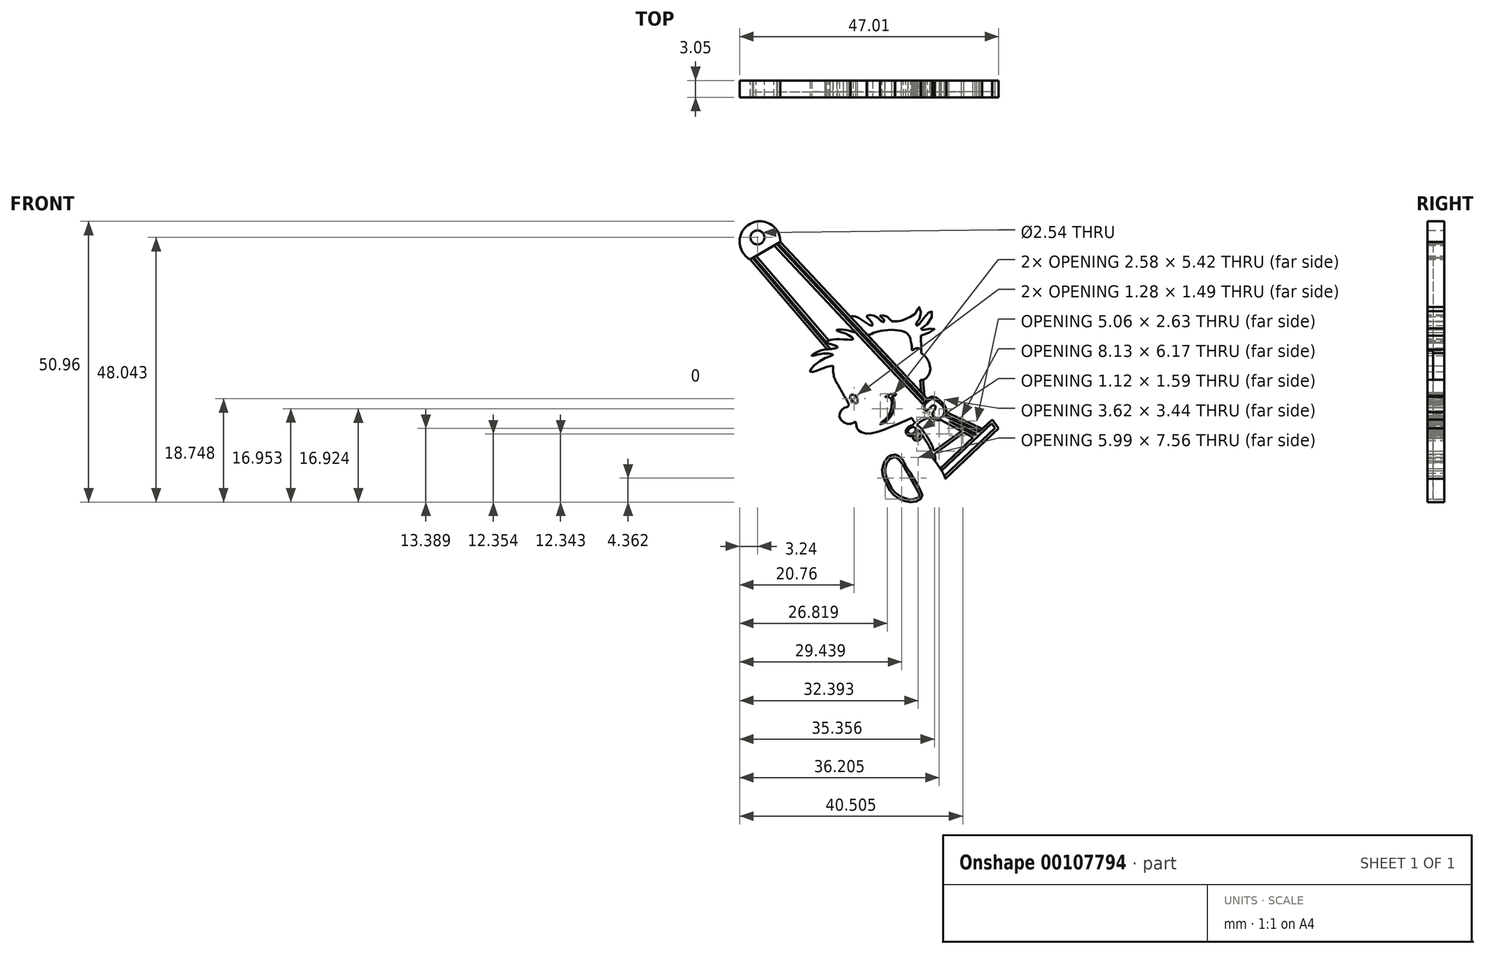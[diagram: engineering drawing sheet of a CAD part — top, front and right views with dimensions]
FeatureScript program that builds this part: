
annotation { "Feature Type Name" : "Feature", "Feature Type Description" : "" }
export const myFeature = defineFeature(function(context is Context, id is Id, definition is map)
    precondition{}
    {
        {
            var Q0;
            Q0=qCreatedBy(makeId("Front.planeOp"),FACE);
            var sketch = newSketch(context, id + "F0", { "sketchPlane" : qUnion([Q0])});
            skLineSegment(sketch, "E0", {"start": v(-64.2, 41.48) * mm, "end": v(-50.25, 25.18) * mm});
            skLineSegment(sketch, "E1", {"start": v(-64.2, 41.48) * mm, "end": v(-58.72, 44.68) * mm});
            skLineSegment(sketch, "E2", {"start": v(-63.09, 42.13) * mm, "end": v(-49.93, 26.76) * mm});
            skLineSegment(sketch, "E3", {"start": v(-58.72, 44.68) * mm, "end": v(-31.98, 16.16) * mm});
            skLineSegment(sketch, "E4", {"start": v(-59.84, 44.02) * mm, "end": v(-32.85, 15.22) * mm});
            skFitSpline(sketch, "E5", {"points": [v(-47.25, 16.86) * mm, v(-48.32, 18.85) * mm, v(-48.92, 20.02) * mm, v(-49.14, 21.44) * mm, v(-49.14, 22.23) * mm], "startDerivative": vector(-3.2, 6.96) * mm, "endDerivative": vector(0.11, 3.82) * mm});
            skFitSpline(sketch, "E6", {"points": [v(-49.14, 22.23) * mm, v(-50.63, 21.88) * mm, v(-53.28, 21.09) * mm, v(-51.32, 23.2) * mm, v(-49.14, 24.21) * mm, v(-51.26, 24.37) * mm, v(-53.02, 24.02) * mm, v(-51.6, 24.88) * mm, v(-50.25, 25.18) * mm], "startDerivative": vector(-10.95, -1.4) * mm, "endDerivative": vector(11.55, 1.04) * mm});
            skFitSpline(sketch, "E7", {"points": [v(-50.63, 26.4) * mm, v(-49.73, 26.15) * mm, v(-48.34, 25.57) * mm, v(-50.25, 25.18) * mm], "startDerivative": vector(2.9, -0.35) * mm, "endDerivative": vector(-7.58, -0.71) * mm});
            skFitSpline(sketch, "E8", {"points": [v(-50.63, 26.4) * mm, v(-49.93, 26.76) * mm, v(-48.12, 27.02) * mm, v(-45.52, 27.03) * mm, v(-46.81, 28) * mm, v(-48.51, 28.64) * mm, v(-47.59, 28.77) * mm, v(-45.03, 28.22) * mm], "startDerivative": vector(6.97, 4.48) * mm, "endDerivative": vector(15.06, -4.13) * mm});
            skFitSpline(sketch, "E9", {"points": [v(-45.97, 31.08) * mm, v(-45.52, 31.23) * mm, v(-44.43, 30.84) * mm, v(-42.05, 29.46) * mm, v(-42.28, 30.32) * mm, v(-43.07, 31.14) * mm, v(-42.61, 31.42) * mm, v(-41.12, 30.96) * mm, v(-40.04, 30.12) * mm, v(-39.85, 30.51) * mm, v(-40.62, 31.22) * mm, v(-39.61, 31.25) * mm, v(-38.58, 30.32) * mm, v(-37.9, 30.27) * mm], "startDerivative": vector(8.3, 3.64) * mm, "endDerivative": vector(15.52, 2.77) * mm});
            skFitSpline(sketch, "E10", {"points": [v(-37.9, 30.27) * mm, v(-37.61, 30.27) * mm, v(-36.65, 30.4) * mm, v(-35.48, 30.9) * mm, v(-34.04, 31.87) * mm, v(-33.6, 32.87) * mm, v(-33.24, 31.32) * mm, v(-34.15, 29.69) * mm, v(-33.9, 29.47) * mm, v(-33.05, 30.35) * mm, v(-31.35, 32.13) * mm, v(-31.6, 30.28) * mm, v(-33.28, 28.7) * mm, v(-30.75, 28.94) * mm, v(-33.2, 27.64) * mm], "startDerivative": vector(6.77, 0.35) * mm, "endDerivative": vector(-29.35, -8.43) * mm});
            skLineSegment(sketch, "E11", {"start": v(-33.2, 27.64) * mm, "end": v(-33.14, 24.45) * mm});
            skLineSegment(sketch, "E12", {"start": v(-33.1, 17.36) * mm, "end": v(-33.32, 19.6) * mm});
            skFitSpline(sketch, "E13", {"points": [v(-31.03, 14.52) * mm, v(-31.53, 13.93) * mm, v(-32.16, 13.58) * mm, v(-32.72, 13.64) * mm, v(-33, 14) * mm, v(-33.04, 14.61) * mm, v(-32.85, 15.22) * mm, v(-32.5, 15.73) * mm, v(-31.98, 16.16) * mm, v(-31.53, 16.47) * mm, v(-31, 16.55) * mm, v(-30.25, 16.3) * mm, v(-29.52, 15.7) * mm, v(-28.84, 14.9) * mm, v(-28.57, 13.8) * mm, v(-28.87, 12.86) * mm, v(-29.59, 12.35) * mm, v(-30.37, 12.34) * mm, v(-31.11, 12.6) * mm, v(-31.51, 13.1) * mm, v(-31.58, 13.55) * mm, v(-31.58, 13.55) * mm], "startDerivative": vector(-8.8, -12.09) * mm, "endDerivative": vector(-0.35, 0.05) * mm});
            skFitSpline(sketch, "E14", {"points": [v(-31.58, 13.55) * mm, v(-31.58, 13.89) * mm], "startDerivative": vector(0, 0.34) * mm, "endDerivative": vector(0, 0.34) * mm});
            skFitSpline(sketch, "E15", {"points": [v(-34.86, 12.73) * mm, v(-36.4, 12.05) * mm, v(-39.9, 10.6) * mm, v(-42.72, 9.88) * mm, v(-44.3, 10.27) * mm, v(-44.78, 10.81) * mm, v(-45, 11.68) * mm, v(-45.12, 12.07) * mm, v(-45.37, 11.84) * mm, v(-46.3, 11.64) * mm, v(-47.24, 11.98) * mm, v(-47.9, 12.75) * mm, v(-47.93, 13.67) * mm, v(-47.24, 14.47) * mm, v(-46.58, 14.72) * mm], "startDerivative": vector(-16.63, -7.69) * mm, "endDerivative": vector(11.77, 2.95) * mm});
            skFitSpline(sketch, "E16", {"points": [v(-31.06, 5.38) * mm, v(-31.8, 7.76) * mm, v(-32.64, 9.09) * mm, v(-33.9, 10.7) * mm, v(-34.71, 11.3) * mm, v(-34.22, 11.91) * mm, v(-33.3, 12.6) * mm, v(-32.58, 12.98) * mm, v(-32.04, 13.21) * mm, v(-31.57, 13.42) * mm], "startDerivative": vector(-4.8, 24.16) * mm, "endDerivative": vector(6.34, 2.68) * mm});
            skFitSpline(sketch, "E17", {"points": [v(-34.86, 12.73) * mm, v(-34.32, 11.83) * mm], "startDerivative": vector(0.58, -0.9) * mm, "endDerivative": vector(0.58, -0.9) * mm});
            skFitSpline(sketch, "E18", {"points": [v(-34.71, 11.3) * mm, v(-35.02, 11.3) * mm, v(-35.4, 11.14) * mm, v(-35.75, 10.78) * mm, v(-35.92, 10.31) * mm, v(-35.8, 9.8) * mm, v(-35.36, 9.47) * mm, v(-34.74, 9.45) * mm, v(-34.21, 9.83) * mm, v(-33.78, 10.6) * mm], "startDerivative": vector(-3.76, 0.6) * mm, "endDerivative": vector(1.87, 5.29) * mm});
            skFitSpline(sketch, "E19", {"points": [v(-34.53, 9.54) * mm, v(-34.61, 9.33) * mm, v(-34.6, 8.92) * mm, v(-34.07, 8.6) * mm, v(-33.39, 8.79) * mm, v(-33.09, 9.22) * mm, v(-32.96, 9.6) * mm], "startDerivative": vector(-0.73, -1.58) * mm, "endDerivative": vector(0.62, 2.36) * mm});
            skFitSpline(sketch, "E20", {"points": [v(-36.39, 4.97) * mm, v(-36.92, 5.54) * mm, v(-37.62, 6.02) * mm, v(-38.5, 6) * mm, v(-39.4, 5.38) * mm, v(-40.07, 4.14) * mm, v(-40.18, 2.57) * mm, v(-39.43, 0.66) * mm, v(-38.4, -1) * mm, v(-36.03, -2.41) * mm, v(-34.07, -2.41) * mm, v(-32.96, -1.61) * mm, v(-33.76, 0.46) * mm, v(-35.06, 2.73) * mm], "startDerivative": vector(-9.48, 10.54) * mm, "endDerivative": vector(-12.52, 22.26) * mm});
            skFitSpline(sketch, "E21", {"points": [v(-31.06, 5.38) * mm, v(-32.2, 6.42) * mm, v(-33.81, 7.82) * mm, v(-35.06, 8.03) * mm, v(-36.06, 7.46) * mm, v(-36.53, 6.44) * mm, v(-36.47, 5.38) * mm, v(-36.39, 4.97) * mm, v(-35.83, 3.84) * mm, v(-35.06, 2.73) * mm, v(-33.93, 1.54) * mm, v(-31.96, 0.37) * mm, v(-30.57, 0) * mm, v(-28.9, 0.46) * mm, v(-28.85, 1.93) * mm, v(-29.63, 3.42) * mm, v(-31.06, 5.38) * mm]});
            skFitSpline(sketch, "E22", {"points": [v(-47.25, 16.86) * mm, v(-46.31, 15.1) * mm, v(-46.58, 14.72) * mm], "startDerivative": vector(2.14, -3.1) * mm, "endDerivative": vector(-1.2, -0.93) * mm});
            skFitSpline(sketch, "E23", {"points": [v(-46, 16.85) * mm, v(-45.77, 16.94) * mm, v(-45.48, 16.94) * mm, v(-45.26, 16.87) * mm, v(-45.05, 16.69) * mm, v(-44.83, 16.37) * mm, v(-44.72, 16.16) * mm, v(-44.67, 15.77) * mm, v(-44.76, 15.51) * mm, v(-44.97, 15.41) * mm, v(-45.3, 15.51) * mm, v(-45.54, 15.69) * mm, v(-45.75, 15.94) * mm, v(-45.91, 16.18) * mm, v(-46.02, 16.45) * mm, v(-46, 16.85) * mm]});
            skFitSpline(sketch, "E24", {"points": [v(-39.76, 16.5) * mm, v(-39.3, 16.83) * mm, v(-38.88, 17.02) * mm, v(-38.42, 17.1) * mm, v(-37.97, 17.1) * mm, v(-37.72, 17.02) * mm, v(-37.8, 16.8) * mm, v(-38.05, 16.7) * mm, v(-38.45, 16.64) * mm, v(-38.26, 16.39) * mm, v(-38.13, 16.08) * mm, v(-38, 15.27) * mm, v(-38.09, 14.33) * mm, v(-38.44, 13.4) * mm, v(-39.06, 12.51) * mm, v(-40.08, 11.73) * mm, v(-40.59, 11.59) * mm, v(-40.52, 11.78) * mm, v(-39.97, 12.18) * mm, v(-39.46, 12.7) * mm, v(-39, 13.31) * mm, v(-38.64, 14.08) * mm, v(-38.5, 15.43) * mm, v(-38.58, 16.15) * mm, v(-39.06, 16.53) * mm, v(-39.76, 16.5) * mm]});
            skLineSegment(sketch, "E25", {"start": v(-19.1, 10.81) * mm, "end": v(-28.78, 1.68) * mm});
            skLineSegment(sketch, "E26", {"start": v(-19.1, 10.81) * mm, "end": v(-20.27, 12.45) * mm});
            skLineSegment(sketch, "E27", {"start": v(-20.27, 12.45) * mm, "end": v(-29.7, 3.55) * mm});
            skLineSegment(sketch, "E28", {"start": v(-23.36, 9.53) * mm, "end": v(-28.13, 12.15) * mm});
            skLineSegment(sketch, "E29", {"start": v(-30.23, 12.31) * mm, "end": v(-30.28, 12.3) * mm});
            skLineSegment(sketch, "E30", {"start": v(-31.79, 7.73) * mm, "end": v(-31.76, 7.73) * mm});
            skLineSegment(sketch, "E31", {"start": v(-31.17, 5.92) * mm, "end": v(-24.94, 10.4) * mm});
            skLineSegment(sketch, "E32", {"start": v(-22.08, 10.74) * mm, "end": v(-28.57, 13.75) * mm});
            skLineSegment(sketch, "E33", {"start": v(-23.07, 9.8) * mm, "end": v(-29.11, 12.6) * mm});
            skLineSegment(sketch, "E34", {"start": v(-29.11, 12.6) * mm, "end": v(-29.02, 12.67) * mm});
            skFitSpline(sketch, "E35.0", {"points": [v(-35.39, 22.53) * mm, v(-35.38, 22.62) * mm, v(-35.36, 22.8) * mm, v(-35.3, 23.1) * mm, v(-35.2, 23.42) * mm, v(-35.02, 23.75) * mm, v(-34.8, 24.07) * mm, v(-34.55, 24.35) * mm, v(-34.33, 24.53) * mm, v(-34.14, 24.62) * mm, v(-34, 24.66) * mm, v(-33.84, 24.67) * mm, v(-33.64, 24.65) * mm, v(-33.4, 24.58) * mm, v(-33.1, 24.43) * mm, v(-32.73, 24.2) * mm, v(-32.41, 23.9) * mm, v(-32.14, 23.54) * mm, v(-31.95, 23.21) * mm, v(-31.78, 22.83) * mm, v(-31.63, 22.41) * mm, v(-31.52, 21.98) * mm, v(-31.49, 21.55) * mm, v(-31.55, 21.16) * mm, v(-31.67, 20.81) * mm, v(-31.82, 20.52) * mm, v(-31.98, 20.28) * mm, v(-32.16, 20.05) * mm, v(-32.37, 19.87) * mm, v(-32.63, 19.72) * mm, v(-32.92, 19.63) * mm, v(-33.26, 19.59) * mm, v(-33.57, 19.58) * mm, v(-33.78, 19.59) * mm, v(-33.9, 19.6) * mm, v(-33.97, 19.6) * mm, v(-33.98, 19.6) * mm, v(-33.98, 19.6) * mm, v(-33.98, 19.6) * mm]});
            skLineSegment(sketch, "E36.0", {"start": v(-63.76, 41.74) * mm, "end": v(-49.64, 25.24) * mm});
            skFitSpline(sketch, "E37.0", {"points": [v(-31.17, 4.74) * mm, v(-31.44, 5.05) * mm, v(-31.68, 5.3) * mm, v(-31.93, 5.52) * mm, v(-32.2, 5.75) * mm, v(-32.5, 6) * mm, v(-32.82, 6.32) * mm, v(-33.14, 6.63) * mm, v(-33.47, 6.94) * mm, v(-33.79, 7.2) * mm, v(-34.08, 7.4) * mm, v(-34.33, 7.5) * mm, v(-34.57, 7.55) * mm, v(-34.8, 7.56) * mm, v(-35.02, 7.52) * mm, v(-35.33, 7.4) * mm, v(-35.6, 7.21) * mm, v(-35.8, 6.98) * mm, v(-35.92, 6.78) * mm, v(-36, 6.56) * mm, v(-36.03, 6.33) * mm, v(-36.04, 6.04) * mm, v(-36, 5.75) * mm, v(-35.98, 5.53) * mm, v(-35.96, 5.38) * mm, v(-35.94, 5.27) * mm, v(-35.93, 5.2) * mm, v(-35.9, 5.11) * mm, v(-35.84, 4.97) * mm, v(-35.74, 4.74) * mm, v(-35.58, 4.43) * mm, v(-35.4, 4.1) * mm, v(-35.16, 3.73) * mm, v(-34.85, 3.3) * mm, v(-34.43, 2.75) * mm, v(-34.04, 2.31) * mm, v(-33.66, 1.98) * mm, v(-33.33, 1.72) * mm, v(-32.96, 1.48) * mm, v(-32.57, 1.24) * mm, v(-32.18, 1.03) * mm, v(-31.8, 0.85) * mm, v(-31.48, 0.71) * mm, v(-31.1, 0.58) * mm, v(-30.74, 0.52) * mm, v(-30.24, 0.51) * mm, v(-29.86, 0.55) * mm, v(-29.59, 0.62) * mm, v(-29.43, 0.69) * mm, v(-29.34, 0.74) * mm, v(-29.3, 0.79) * mm, v(-29.27, 0.83) * mm, v(-29.24, 0.9) * mm, v(-29.22, 1.03) * mm, v(-29.22, 1.27) * mm, v(-29.28, 1.6) * mm, v(-29.39, 1.93) * mm, v(-29.51, 2.23) * mm, v(-29.67, 2.53) * mm, v(-29.86, 2.85) * mm, v(-30.09, 3.2) * mm, v(-30.43, 3.72) * mm, v(-30.8, 4.26) * mm, v(-31.17, 4.74) * mm, v(-31.44, 5.05) * mm, v(-31.68, 5.3) * mm, v(-31.17, 4.74) * mm]});
            skFitSpline(sketch, "E38.0", {"points": [v(-36.76, 4.63) * mm, v(-36.86, 4.74) * mm, v(-37, 4.9) * mm, v(-37.2, 5.1) * mm, v(-37.36, 5.26) * mm, v(-37.51, 5.38) * mm, v(-37.66, 5.48) * mm, v(-37.77, 5.54) * mm, v(-37.85, 5.56) * mm, v(-37.98, 5.59) * mm, v(-38.22, 5.58) * mm, v(-38.55, 5.45) * mm, v(-38.9, 5.2) * mm, v(-39.2, 4.83) * mm, v(-39.46, 4.36) * mm, v(-39.65, 3.84) * mm, v(-39.72, 3.4) * mm, v(-39.73, 3.03) * mm, v(-39.7, 2.75) * mm, v(-39.64, 2.47) * mm, v(-39.54, 2.16) * mm, v(-39.42, 1.84) * mm, v(-39.27, 1.5) * mm, v(-39.12, 1.18) * mm, v(-38.96, 0.84) * mm, v(-38.8, 0.52) * mm, v(-38.6, 0.12) * mm, v(-38.4, -0.23) * mm, v(-38.13, -0.56) * mm, v(-37.8, -0.89) * mm, v(-37.28, -1.3) * mm, v(-36.67, -1.63) * mm, v(-36.18, -1.83) * mm, v(-35.83, -1.95) * mm, v(-35.5, -2.01) * mm, v(-35.2, -2.05) * mm, v(-34.89, -2.05) * mm, v(-34.6, -2.01) * mm, v(-34.3, -1.95) * mm, v(-34, -1.86) * mm, v(-33.74, -1.76) * mm, v(-33.56, -1.64) * mm, v(-33.48, -1.55) * mm, v(-33.46, -1.5) * mm, v(-33.45, -1.48) * mm, v(-33.44, -1.43) * mm, v(-33.45, -1.32) * mm, v(-33.5, -1.11) * mm, v(-33.63, -0.8) * mm, v(-33.82, -0.44) * mm, v(-34.04, -0.06) * mm, v(-34.35, 0.45) * mm, v(-34.7, 1.07) * mm, v(-35.11, 1.79) * mm, v(-35.37, 2.25) * mm, v(-35.5, 2.48) * mm]});
            skFitSpline(sketch, "E39", {"points": [v(-36.76, 4.63) * mm, v(-36.13, 3.59) * mm, v(-35.5, 2.48) * mm], "startDerivative": vector(1.28, -2.1) * mm, "endDerivative": vector(1.24, -2.2) * mm});
            skFitSpline(sketch, "E40.0", {"points": [v(-35.08, 13.18) * mm, v(-35.25, 13.1) * mm, v(-35.58, 12.95) * mm, v(-36.1, 12.72) * mm, v(-36.74, 12.44) * mm, v(-37.53, 12.11) * mm, v(-38.4, 11.75) * mm, v(-39.3, 11.38) * mm, v(-40.18, 11.03) * mm, v(-41, 10.73) * mm, v(-41.74, 10.5) * mm, v(-42.3, 10.4) * mm, v(-42.71, 10.37) * mm, v(-43.1, 10.4) * mm, v(-43.48, 10.46) * mm, v(-43.78, 10.57) * mm, v(-43.97, 10.65) * mm, v(-44.1, 10.74) * mm, v(-44.2, 10.81) * mm, v(-44.26, 10.9) * mm, v(-44.31, 11) * mm, v(-44.37, 11.15) * mm, v(-44.42, 11.33) * mm, v(-44.46, 11.5) * mm, v(-44.49, 11.64) * mm, v(-44.5, 11.74) * mm, v(-44.52, 11.85) * mm, v(-44.54, 11.94) * mm, v(-44.56, 12.01) * mm, v(-44.57, 12.07) * mm, v(-44.59, 12.13) * mm, v(-44.6, 12.2) * mm, v(-44.64, 12.28) * mm, v(-44.69, 12.35) * mm, v(-44.74, 12.41) * mm, v(-44.82, 12.48) * mm, v(-44.95, 12.55) * mm, v(-45.1, 12.58) * mm, v(-45.25, 12.56) * mm, v(-45.35, 12.52) * mm, v(-45.44, 12.47) * mm, v(-45.5, 12.42) * mm, v(-45.55, 12.37) * mm, v(-45.58, 12.33) * mm, v(-45.61, 12.3) * mm, v(-45.64, 12.27) * mm, v(-45.67, 12.24) * mm, v(-45.68, 12.23) * mm, v(-45.73, 12.2) * mm, v(-45.83, 12.17) * mm, v(-46, 12.14) * mm, v(-46.18, 12.13) * mm, v(-46.43, 12.15) * mm, v(-46.64, 12.21) * mm, v(-46.85, 12.32) * mm, v(-47.05, 12.45) * mm, v(-47.29, 12.67) * mm, v(-47.43, 12.9) * mm, v(-47.5, 13.09) * mm, v(-47.5, 13.22) * mm, v(-47.5, 13.35) * mm, v(-47.47, 13.47) * mm, v(-47.4, 13.61) * mm, v(-47.26, 13.8) * mm, v(-47.02, 14.03) * mm, v(-46.78, 14.15) * mm, v(-46.58, 14.2) * mm, v(-46.46, 14.23) * mm]});
            skFitSpline(sketch, "E41.0", {"points": [v(-46.84, 17.14) * mm, v(-46.75, 17.01) * mm, v(-46.57, 16.75) * mm, v(-46.31, 16.37) * mm, v(-46.09, 16) * mm, v(-45.94, 15.69) * mm, v(-45.85, 15.44) * mm, v(-45.82, 15.28) * mm, v(-45.8, 15.13) * mm, v(-45.82, 14.98) * mm, v(-45.86, 14.8) * mm, v(-45.97, 14.6) * mm, v(-46.12, 14.44) * mm, v(-46.22, 14.36) * mm, v(-46.27, 14.32) * mm]});
            skFitSpline(sketch, "E42", {"points": [v(-46.46, 14.23) * mm, v(-46.35, 14.26) * mm, v(-46.27, 14.32) * mm], "startDerivative": vector(0.22, 0.05) * mm, "endDerivative": vector(0.15, 0.14) * mm});
            skFitSpline(sketch, "E43.0", {"points": [v(-46.79, 17.07) * mm, v(-46.92, 17.37) * mm, v(-47.22, 17.96) * mm, v(-47.6, 18.62) * mm, v(-47.87, 19.1) * mm, v(-48.06, 19.4) * mm, v(-48.22, 19.67) * mm, v(-48.35, 19.92) * mm, v(-48.44, 20.18) * mm, v(-48.52, 20.48) * mm, v(-48.58, 20.81) * mm, v(-48.62, 21.15) * mm, v(-48.64, 21.47) * mm, v(-48.64, 21.74) * mm, v(-48.64, 21.98) * mm, v(-48.64, 22.13) * mm, v(-48.63, 22.21) * mm]});
            skLineSegment(sketch, "E44.0", {"start": v(-63.53, 41.87) * mm, "end": v(-50.4, 26.54) * mm});
            skLineSegment(sketch, "E45.0", {"start": v(-59.4, 44.29) * mm, "end": v(-32.56, 15.66) * mm});
            skLineSegment(sketch, "E46.0", {"start": v(-59.16, 44.42) * mm, "end": v(-32.37, 15.84) * mm});
            skFitSpline(sketch, "E47.0", {"points": [v(-34.88, 22.47) * mm, v(-34.87, 22.56) * mm, v(-34.85, 22.73) * mm, v(-34.81, 22.93) * mm, v(-34.76, 23.09) * mm, v(-34.71, 23.21) * mm, v(-34.65, 23.34) * mm, v(-34.55, 23.53) * mm, v(-34.39, 23.75) * mm, v(-34.18, 23.99) * mm, v(-34, 24.12) * mm, v(-33.92, 24.15) * mm, v(-33.85, 24.16) * mm, v(-33.78, 24.15) * mm, v(-33.7, 24.13) * mm, v(-33.55, 24.08) * mm, v(-33.36, 23.98) * mm, v(-33.12, 23.83) * mm, v(-32.92, 23.67) * mm, v(-32.74, 23.49) * mm, v(-32.58, 23.26) * mm, v(-32.41, 22.97) * mm, v(-32.25, 22.63) * mm, v(-32.12, 22.26) * mm, v(-32.05, 21.96) * mm, v(-32.02, 21.73) * mm, v(-32.02, 21.57) * mm, v(-32.03, 21.43) * mm, v(-32.07, 21.24) * mm, v(-32.13, 21.07) * mm, v(-32.2, 20.9) * mm, v(-32.3, 20.75) * mm, v(-32.4, 20.57) * mm, v(-32.54, 20.4) * mm, v(-32.67, 20.29) * mm, v(-32.83, 20.2) * mm, v(-33.02, 20.14) * mm, v(-33.29, 20.1) * mm, v(-33.57, 20.1) * mm, v(-33.77, 20.1) * mm, v(-33.88, 20.1) * mm, v(-33.94, 20.1) * mm, v(-33.95, 20.11) * mm, v(-33.96, 20.11) * mm, v(-33.96, 20.11) * mm]});
            skLineSegment(sketch, "E48.0", {"start": v(-32.53, 16.75) * mm, "end": v(-32.8, 19.67) * mm});
            skFitSpline(sketch, "E49.0", {"points": [v(-34.43, 13.01) * mm, v(-34.22, 12.68) * mm, v(-34.06, 12.38) * mm, v(-33.89, 12.11) * mm]});
            skLineSegment(sketch, "E50", {"start": v(-35.08, 13.18) * mm, "end": v(-34.67, 13.38) * mm});
            skLineSegment(sketch, "E51", {"start": v(-34.67, 13.38) * mm, "end": v(-34.43, 13.01) * mm});
            skLineSegment(sketch, "E52.0", {"start": v(-19.77, 10.88) * mm, "end": v(-28.95, 2.21) * mm});
            skLineSegment(sketch, "E53.0", {"start": v(-19.77, 10.88) * mm, "end": v(-20.35, 11.69) * mm});
            skLineSegment(sketch, "E54.0", {"start": v(-20.35, 11.69) * mm, "end": v(-29.43, 3.12) * mm});
            skLineSegment(sketch, "E55.0", {"start": v(-22.68, 10.17) * mm, "end": v(-28.78, 13) * mm});
            skLineSegment(sketch, "E56.0", {"start": v(-22.48, 10.36) * mm, "end": v(-28.67, 13.24) * mm});
            skLineSegment(sketch, "E57", {"start": v(-35.39, 22.53) * mm, "end": v(-34.88, 22.47) * mm});
            skLineSegment(sketch, "E58", {"start": v(-33.9, 20.1) * mm, "end": v(-33.93, 19.6) * mm});
            skLineSegment(sketch, "E59.0", {"start": v(-23.75, 9.17) * mm, "end": v(-29.55, 12.36) * mm});
            skFitSpline(sketch, "E60", {"points": [v(-48.63, 22.21) * mm, v(-48.28, 23.12) * mm, v(-47.16, 24.87) * mm, v(-43.94, 27.05) * mm], "startDerivative": vector(1.37, 3.74) * mm, "endDerivative": vector(8.2, 4.6) * mm});
            skFitSpline(sketch, "E61", {"points": [v(-42.77, 27.66) * mm, v(-41.53, 28.26) * mm, v(-38.17, 28.71) * mm, v(-35.73, 28.07) * mm, v(-35.12, 27.05) * mm, v(-34.81, 25.09) * mm, v(-34.78, 24.08) * mm, v(-34.78, 24.07) * mm], "startDerivative": vector(7.3, 4.3) * mm, "endDerivative": vector(-0.23, -0.13) * mm});
            skFitSpline(sketch, "E62", {"points": [v(-33.97, 11.44) * mm, v(-33.26, 12.06) * mm, v(-32.47, 12.47) * mm, v(-31.62, 12.83) * mm, v(-31.42, 12.88) * mm], "startDerivative": vector(2.4, 2.33) * mm, "endDerivative": vector(1.2, 0.2) * mm});
            skFitSpline(sketch, "E63", {"points": [v(-33.97, 11.44) * mm, v(-33.28, 10.95) * mm, v(-32.68, 10.22) * mm, v(-32.04, 9.27) * mm, v(-31.27, 7.92) * mm, v(-30.9, 6.88) * mm, v(-30.75, 6.22) * mm], "startDerivative": vector(4.77, -2.94) * mm, "endDerivative": vector(1.04, -4.64) * mm});
            skLineSegment(sketch, "E64", {"start": v(-30.86, 6.7) * mm, "end": v(-25.84, 10.32) * mm});
            skFitSpline(sketch, "E65", {"points": [v(-34.53, 11.1) * mm, v(-34.95, 11) * mm, v(-35.39, 10.7) * mm, v(-35.52, 10.14) * mm, v(-35.24, 9.85) * mm, v(-34.82, 9.8) * mm, v(-34.42, 10.13) * mm, v(-34.14, 10.6) * mm, v(-34.05, 10.8) * mm], "startDerivative": vector(-3.4, -0.51) * mm, "endDerivative": vector(0.72, 2.16) * mm});
            skFitSpline(sketch, "E66", {"points": [v(-30.75, 6.22) * mm, v(-30.59, 5.46) * mm, v(-30.62, 4.86) * mm], "startDerivative": vector(0.4, -1.47) * mm, "endDerivative": vector(-0.18, -1.26) * mm});
            skFitSpline(sketch, "E67", {"points": [v(-33.16, 9.88) * mm, v(-33.46, 9.3) * mm, v(-33.87, 9) * mm, v(-34.24, 9.18) * mm, v(-34.21, 9.83) * mm], "startDerivative": vector(-0.92, -2.27) * mm, "endDerivative": vector(0.62, 2.73) * mm});
            skFitSpline(sketch, "E68", {"points": [v(-32.56, 14.6) * mm, v(-32.45, 15.16) * mm, v(-31.53, 16.02) * mm, v(-31, 16.14) * mm, v(-30.2, 15.7) * mm, v(-29.26, 14.86) * mm, v(-28.95, 13.88) * mm, v(-29.3, 12.99) * mm, v(-29.86, 12.65) * mm], "startDerivative": vector(-1.73, 6.06) * mm, "endDerivative": vector(-5.5, -2.27) * mm});
            skFitSpline(sketch, "E69", {"points": [v(-32.56, 14.6) * mm, v(-32.56, 14.13) * mm, v(-32.17, 14.03) * mm, v(-31.7, 14.39) * mm, v(-31.24, 14.87) * mm, v(-31, 15.01) * mm, v(-30.58, 14.88) * mm, v(-30.56, 14.48) * mm, v(-30.8, 14.05) * mm, v(-31.06, 13.69) * mm, v(-31.06, 13.2) * mm, v(-30.47, 12.74) * mm, v(-29.86, 12.65) * mm], "startDerivative": vector(-1.48, -6.54) * mm, "endDerivative": vector(6.39, -0.19) * mm});
            skLineSegment(sketch, "E70", {"start": v(-25.84, 10.32) * mm, "end": v(-25.39, 10.64) * mm});
            skLineSegment(sketch, "E71", {"start": v(-30.86, 6.7) * mm, "end": v(-31.28, 6.4) * mm});
            skPoint(sketch, "E72", {"position": v(-25.4, 10.07) * mm});
            skFitSpline(sketch, "E73", {"points": [v(-34.8, 24.94) * mm, v(-34.25, 25.3) * mm, v(-33.75, 25.39) * mm, v(-33.16, 25.14) * mm], "startDerivative": vector(1.57, 1.2) * mm, "endDerivative": vector(1.76, -0.94) * mm});
            skArc(sketch, "E74", {"start": v(-58.72, 44.68) * mm, "mid": v(-64.28, 47.9) * mm, "end": v(-64.2, 41.48) * mm});
            skCircle(sketch, "E75", {"center": v(-62.87, 45.5) * mm, "radius": 1.27 * mm});
            skFitSpline(sketch, "E76", {"points": [v(-50.4, 26.36) * mm, v(-50.52, 26.36) * mm, v(-50.58, 26.34) * mm], "startDerivative": vector(-0.23, 0.02) * mm, "endDerivative": vector(-0.13, -0.06) * mm});
            skSolve(sketch);
        }
        {
            var Q0;
            {var subQ3=sQuery(id+"F0.wireOp",EDGE,"E44.0");Q0=makeQuery(id+"F0.imprint","IMPRINT",FACE,{"disambiguationData":[TD([[makeQuery(id+"F0.imprint","IMPRINT",EDGE,{"derivedFrom":subQ3}),-1.0]])]});}
            var Q1;
            {var subQ0=sQuery(id+"F0.wireOp",EDGE,"E45.0");Q1=makeQuery(id+"F0.imprint","IMPRINT",FACE,{"disambiguationData":[TD([[makeQuery(id+"F0.imprint","IMPRINT",EDGE,{"derivedFrom":subQ0}),1.0]])]});}
            var Q2;
            {var subQ0=sQuery(id+"F0.wireOp",EDGE,"E28");var subQ3=sQuery(id+"F0.wireOp",EDGE,"E27");var subQ4=makeQuery(id+"F0.imprint","INTERSECT",VERTEX,{"derivedFrom":[subQ3,subQ0]});Q2=makeQuery(id+"F0.imprint","IMPRINT",FACE,{"disambiguationData":[TD([[makeQuery(id+"F0.imprint","IMPRINT",EDGE,{"disambiguationData":[TD([[subQ4,1.0]])],"derivedFrom":subQ3}),-1.0]])]});}
            var Q3;
            {var subQ0=sQuery(id+"F0.wireOp",EDGE,"E55.0");Q3=makeQuery(id+"F0.imprint","IMPRINT",FACE,{"disambiguationData":[TD([[makeQuery(id+"F0.imprint","IMPRINT",EDGE,{"derivedFrom":subQ0}),-1.0]])]});}
            var Q4;
            {var subQ6=sQuery(id+"F0.wireOp",EDGE,"E14");Q4=makeQuery(id+"F0.imprint","IMPRINT",FACE,{"disambiguationData":[TD([[makeQuery(id+"F0.imprint","IMPRINT",EDGE,{"derivedFrom":subQ6}),1.0]])]});}
            var Q5;
            Q5=makeQuery(id+"F0.imprint","IMPRINT",FACE,{"disambiguationData":[TD([[makeQuery(id+"F0.imprint","IMPRINT",EDGE,{"derivedFrom":sQuery(id+"F0.wireOp",EDGE,"E68")}),-1.0]])]});
            var Q6;
            {var subQ3=sQuery(id+"F0.wireOp",EDGE,"E67");Q6=makeQuery(id+"F0.imprint","IMPRINT",FACE,{"disambiguationData":[TD([[makeQuery(id+"F0.imprint","IMPRINT",EDGE,{"derivedFrom":subQ3}),-1.0]])]});}
            var Q7;
            Q7=makeQuery(id+"F0.imprint","IMPRINT",FACE,{"disambiguationData":[TD([[makeQuery(id+"F0.imprint","IMPRINT",EDGE,{"derivedFrom":sQuery(id+"F0.wireOp",EDGE,"E37.0")}),1.0]])]});
            var Q8;
            Q8=makeQuery(id+"F0.imprint","IMPRINT",FACE,{"disambiguationData":[TD([[makeQuery(id+"F0.imprint","IMPRINT",EDGE,{"derivedFrom":sQuery(id+"F0.wireOp",EDGE,"E38.0")}),1.0]])]});
            var Q9;
            {var subQ0=sQuery(id+"F0.wireOp",EDGE,"E52.0");Q9=makeQuery(id+"F0.imprint","IMPRINT",FACE,{"disambiguationData":[TD([[makeQuery(id+"F0.imprint","IMPRINT",EDGE,{"derivedFrom":subQ0}),-1.0]])]});}
            var Q10;
            {var subQ5=sQuery(id+"F0.wireOp",EDGE,"E66");Q10=makeQuery(id+"F0.imprint","IMPRINT",FACE,{"disambiguationData":[TD([[makeQuery(id+"F0.imprint","IMPRINT",EDGE,{"derivedFrom":subQ5}),1.0]])]});}
            var Q11;
            {var subQ0=sQuery(id+"F0.wireOp",EDGE,"E62");Q11=makeQuery(id+"F0.imprint","IMPRINT",FACE,{"disambiguationData":[TD([[makeQuery(id+"F0.imprint","IMPRINT",EDGE,{"derivedFrom":subQ0}),-1.0]])]});}
            var Q12;
            {var subQ6=sQuery(id+"F0.wireOp",EDGE,"E12");Q12=makeQuery(id+"F0.imprint","IMPRINT",FACE,{"disambiguationData":[TD([[makeQuery(id+"F0.imprint","IMPRINT",EDGE,{"derivedFrom":subQ6}),1.0]])]});}
            var Q13;
            {var subQ0=sQuery(id+"F0.wireOp",EDGE,"E65");Q13=makeQuery(id+"F0.imprint","IMPRINT",FACE,{"disambiguationData":[TD([[makeQuery(id+"F0.imprint","IMPRINT",EDGE,{"derivedFrom":subQ0}),1.0]])]});}
            var Q14;
            {var subQ0=sQuery(id+"F0.wireOp",EDGE,"E36.0");var subQ1=sQuery(id+"F0.wireOp",EDGE,"E7");var subQ2=makeQuery(id+"F0.imprint","INTERSECT",VERTEX,{"disambiguationData":[OD(0.0)],"derivedFrom":[subQ1,subQ0]});Q14=makeQuery(id+"F0.imprint","IMPRINT",FACE,{"disambiguationData":[TD([[makeQuery(id+"F0.imprint","IMPRINT",EDGE,{"disambiguationData":[TD([[subQ2,1.0]])],"derivedFrom":subQ1}),-1.0]])]});}
            var Q15;
            {var subQ3=sQuery(id+"F0.wireOp",EDGE,"E73");Q15=makeQuery(id+"F0.imprint","IMPRINT",FACE,{"disambiguationData":[TD([[makeQuery(id+"F0.imprint","IMPRINT",EDGE,{"derivedFrom":subQ3}),-1.0]])]});}
            extrude(context, id + "F1", {"entities" : qUnion([Q0, Q1, Q2, Q3, Q4, Q5, Q6, Q7, Q8, Q9, Q10, Q11, Q12, Q13, Q14, Q15]), "depth" : 2.03 * mm});
        }
        {
            var Q0;
            Q0=makeQuery(id+"F0.imprint","IMPRINT",FACE,{"disambiguationData":[TD([[makeQuery(id+"F0.imprint","IMPRINT",EDGE,{"derivedFrom":sQuery(id+"F0.wireOp",EDGE,"E5")}),-1.0]])]});
            var Q1;
            {var subQ0=sQuery(id+"F0.wireOp",EDGE,"E20");Q1=makeQuery(id+"F0.imprint","IMPRINT",FACE,{"disambiguationData":[TD([[makeQuery(id+"F0.imprint","IMPRINT",EDGE,{"derivedFrom":subQ0}),1.0]])]});}
            var Q2;
            Q2=makeQuery(id+"F0.imprint","IMPRINT",FACE,{"disambiguationData":[TD([[makeQuery(id+"F0.imprint","IMPRINT",EDGE,{"derivedFrom":sQuery(id+"F0.wireOp",EDGE,"E37.0")}),-1.0]])]});
            var Q3;
            {var subQ7=sQuery(id+"F0.wireOp",EDGE,"E25");Q3=makeQuery(id+"F0.imprint","IMPRINT",FACE,{"disambiguationData":[TD([[makeQuery(id+"F0.imprint","IMPRINT",EDGE,{"derivedFrom":subQ7}),-1.0]])]});}
            var Q4;
            {var subQ5=sQuery(id+"F0.wireOp",EDGE,"E64");Q4=makeQuery(id+"F0.imprint","IMPRINT",FACE,{"disambiguationData":[TD([[makeQuery(id+"F0.imprint","IMPRINT",EDGE,{"derivedFrom":subQ5}),-1.0]])]});}
            var Q5;
            {var subQ12=sQuery(id+"F0.wireOp",EDGE,"E62");Q5=makeQuery(id+"F0.imprint","IMPRINT",FACE,{"disambiguationData":[TD([[makeQuery(id+"F0.imprint","IMPRINT",EDGE,{"derivedFrom":subQ12}),1.0]])]});}
            var Q6;
            {var subQ5=sQuery(id+"F0.wireOp",EDGE,"E66");Q6=makeQuery(id+"F0.imprint","IMPRINT",FACE,{"disambiguationData":[TD([[makeQuery(id+"F0.imprint","IMPRINT",EDGE,{"derivedFrom":subQ5}),-1.0]])]});}
            var Q7;
            {var subQ3=sQuery(id+"F0.wireOp",EDGE,"E71");Q7=makeQuery(id+"F0.imprint","IMPRINT",FACE,{"disambiguationData":[TD([[makeQuery(id+"F0.imprint","IMPRINT",EDGE,{"derivedFrom":subQ3}),1.0]])]});}
            var Q8;
            {var subQ10=sQuery(id+"F0.wireOp",EDGE,"E14");Q8=makeQuery(id+"F0.imprint","IMPRINT",FACE,{"disambiguationData":[TD([[makeQuery(id+"F0.imprint","IMPRINT",EDGE,{"derivedFrom":subQ10}),-1.0]])]});}
            var Q9;
            {var subQ3=sQuery(id+"F0.wireOp",EDGE,"E70");Q9=makeQuery(id+"F0.imprint","IMPRINT",FACE,{"disambiguationData":[TD([[makeQuery(id+"F0.imprint","IMPRINT",EDGE,{"derivedFrom":subQ3}),1.0]])]});}
            var Q10;
            {var subQ5=sQuery(id+"F0.wireOp",EDGE,"E65");Q10=makeQuery(id+"F0.imprint","IMPRINT",FACE,{"disambiguationData":[TD([[makeQuery(id+"F0.imprint","IMPRINT",EDGE,{"derivedFrom":subQ5}),-1.0]])]});}
            var Q11;
            {var subQ0=sQuery(id+"F0.wireOp",EDGE,"E19");Q11=makeQuery(id+"F0.imprint","IMPRINT",FACE,{"disambiguationData":[TD([[makeQuery(id+"F0.imprint","IMPRINT",EDGE,{"derivedFrom":subQ0}),1.0]])]});}
            var Q12;
            {var subQ3=sQuery(id+"F0.wireOp",EDGE,"E70");Q12=makeQuery(id+"F0.imprint","IMPRINT",FACE,{"disambiguationData":[TD([[makeQuery(id+"F0.imprint","IMPRINT",EDGE,{"derivedFrom":subQ3}),-1.0]])]});}
            var Q13;
            {var subQ0=sQuery(id+"F0.wireOp",EDGE,"E28");var subQ1=sQuery(id+"F0.wireOp",EDGE,"E27");var subQ2=makeQuery(id+"F0.imprint","INTERSECT",VERTEX,{"derivedFrom":[subQ1,subQ0]});Q13=makeQuery(id+"F0.imprint","IMPRINT",FACE,{"disambiguationData":[TD([[makeQuery(id+"F0.imprint","IMPRINT",EDGE,{"disambiguationData":[TD([[subQ2,-1.0]])],"derivedFrom":subQ1}),-1.0]])]});}
            var Q14;
            {var subQ6=sQuery(id+"F0.wireOp",EDGE,"E55.0");Q14=makeQuery(id+"F0.imprint","IMPRINT",FACE,{"disambiguationData":[TD([[makeQuery(id+"F0.imprint","IMPRINT",EDGE,{"derivedFrom":subQ6}),1.0]])]});}
            var Q15;
            {var subQ3=sQuery(id+"F0.wireOp",EDGE,"E9");Q15=makeQuery(id+"F0.imprint","IMPRINT",FACE,{"disambiguationData":[TD([[makeQuery(id+"F0.imprint","IMPRINT",EDGE,{"derivedFrom":subQ3}),-1.0]])]});}
            var Q16;
            Q16=makeQuery(id+"F0.imprint","IMPRINT",FACE,{"disambiguationData":[TD([[makeQuery(id+"F0.imprint","IMPRINT",EDGE,{"derivedFrom":sQuery(id+"F0.wireOp",EDGE,"E47.0")}),1.0]])]});
            var Q17;
            {var subQ5=sQuery(id+"F0.wireOp",EDGE,"E74");Q17=makeQuery(id+"F0.imprint","IMPRINT",FACE,{"disambiguationData":[TD([[makeQuery(id+"F0.imprint","IMPRINT",EDGE,{"derivedFrom":subQ5}),1.0]])]});}
            extrude(context, id + "F2", {"entities" : qUnion([Q0, Q1, Q2, Q3, Q4, Q5, Q6, Q7, Q8, Q9, Q10, Q11, Q12, Q13, Q14, Q15, Q16, Q17]), "depth" : 3.05 * mm});
        }
        {
            var Q0;
            {var subQ4=sQuery(id+"F0.wireOp",EDGE,"e0f1555b-cc6c-473e-9b0f-2676cacd5dec");Q0=makeQuery(id+"F0.imprint","IMPRINT",FACE,{"disambiguationData":[TD([[makeQuery(id+"F0.imprint","IMPRINT",EDGE,{"derivedFrom":subQ4}),1.0]])]});}
            var Q1;
            {var subQ6=sQuery(id+"F0.wireOp",EDGE,"E46.0");Q1=makeQuery(id+"F0.imprint","IMPRINT",FACE,{"disambiguationData":[TD([[makeQuery(id+"F0.imprint","IMPRINT",EDGE,{"derivedFrom":subQ6}),1.0]])]});}
            var Q2;
            {var subQ6=sQuery(id+"F0.wireOp",EDGE,"E45.0");Q2=makeQuery(id+"F0.imprint","IMPRINT",FACE,{"disambiguationData":[TD([[makeQuery(id+"F0.imprint","IMPRINT",EDGE,{"derivedFrom":subQ6}),-1.0]])]});}
            var Q3;
            {var subQ0=sQuery(id+"F0.wireOp",EDGE,"E2");Q3=makeQuery(id+"F0.imprint","IMPRINT",FACE,{"disambiguationData":[TD([[makeQuery(id+"F0.imprint","IMPRINT",EDGE,{"derivedFrom":subQ0}),-1.0]])]});}
            var Q4;
            {var subQ1=sQuery(id+"F0.wireOp",EDGE,"E0");Q4=makeQuery(id+"F0.imprint","IMPRINT",FACE,{"disambiguationData":[TD([[makeQuery(id+"F0.imprint","IMPRINT",EDGE,{"derivedFrom":subQ1}),1.0]])]});}
            extrude(context, id + "F3", {"entities" : qUnion([Q0, Q1, Q2, Q3, Q4]), "depth" : 3.05 * mm});
        }
        {
            var Q0;
            {var subQ0=sQuery(id+"F0.wireOp",EDGE,"E12");Q0=makeQuery(id+"F0.imprint","IMPRINT",FACE,{"disambiguationData":[TD([[makeQuery(id+"F0.imprint","IMPRINT",EDGE,{"derivedFrom":subQ0}),-1.0]])]});}
            var Q1;
            Q1=makeQuery(id+"F0.imprint","IMPRINT",FACE,{"disambiguationData":[TD([[makeQuery(id+"F0.imprint","IMPRINT",EDGE,{"derivedFrom":sQuery(id+"F0.wireOp",EDGE,"E24")}),-1.0]])]});
            var Q2;
            Q2=makeQuery(id+"F0.imprint","IMPRINT",FACE,{"disambiguationData":[TD([[makeQuery(id+"F0.imprint","IMPRINT",EDGE,{"derivedFrom":sQuery(id+"F0.wireOp",EDGE,"E23")}),-1.0]])]});
            var Q3;
            {var subQ0=sQuery(id+"F0.wireOp",EDGE,"E32");Q3=makeQuery(id+"F0.imprint","IMPRINT",FACE,{"disambiguationData":[TD([[makeQuery(id+"F0.imprint","IMPRINT",EDGE,{"derivedFrom":subQ0}),1.0]])]});}
            extrude(context, id + "F4", {"entities" : qUnion([Q0, Q1, Q2, Q3]), "depth" : 3.05 * mm});
        }
        {
            var Q0;
            {var subQ3=sQuery(id+"F0.wireOp",EDGE,"E76");Q0=makeQuery(id+"F0.imprint","IMPRINT",FACE,{"disambiguationData":[TD([[makeQuery(id+"F0.imprint","IMPRINT",EDGE,{"derivedFrom":subQ3}),-1.0]])]});}
            extrude(context, id + "F5", {"entities" : qUnion([Q0]), "depth" : 3.05 * mm});
        }
    });
